# Revit family: P200921MX-080c_MED6200KW
name_source: partatom
category: Specialty Equipment
units: mm (PartAtom-declared; Revit-internal decimal feet)

## family parameters
Always vertical = Yes
Cut with Voids When Loaded = No
Enable Cutting in Views = No
Maintain Annotation Orientation = No
Part Type = Normal
Room Calculation Point = No
Round Connector Dimension = Use Diameter
Shared = No
Work Plane-Based = No

## types (1)
- MED6200KW
    Amps = 0 A
    Back Panel Material = ARCAT - Metal - Aluminum
    Body Material = ARCAT - Metal - Steel - White
    Clearance Material = ARCAT - Clearance
    Default Elevation = 0"
    Depth = 28 3/8"
    Description = Top Load Electric Dryer with Moisture Sensing - 7.0 cu. ft.
    Dimension Guide = https://www.whirlpool.com
    Display Panel Material = ARCAT - Glass - Tempered - Dark Black
    Door Material = ARCAT - Metal - Steel - Stainless
    Family Name = Laundry
    Feature 1 = Moisture Sensing
    Feature 2 = Quick Dry cycle
    Feature 3 = Wrinkle Prevent option
    Handle Material = ARCAT - Metal - Steel - White
    Height = 40 11/16"
    Knob Material = ARCAT - Metal - Steel - Stainless
    Leg Material = ARCAT - Metal - Steel - Stainless
    Manufacturer = Maytag
    Model = MEDC465HW
    Voltage = 0 V
    Width = 29"

## geometry (parser evidence)
native form markers: Sweep x5
no freeform markers — native parametric forms only
